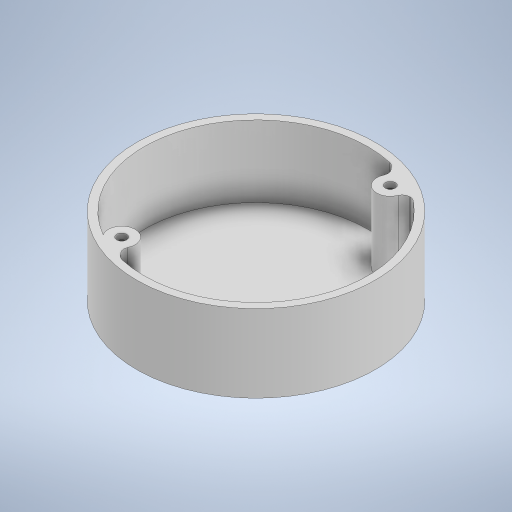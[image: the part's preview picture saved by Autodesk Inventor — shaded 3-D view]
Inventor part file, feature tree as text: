
AUTODESK INVENTOR PART (.ipt)
format: ipt  version: 2023 (Build 270158000, 158)  size: 305,152 bytes
history: native  units: in
note: dims shown in document units (in); Inventor stores cm internally (conversion verified against a paired STEP export)
features: sketch x7, extrude x5, fillet x3, hole x1
ambient origin geometry x8: Origin, YZ Plane, XZ Plane, XY Plane, X Axis, Y Axis, Z Axis, Center Point
bodies: Solid1 (feature_tree)
feature tree (16):
  extrude  "Extrusion1"  Depth=0.1in TaperAngle=0.0deg
  extrude  "Extrusion2"  Depth=4.0in
  extrude  "Extrusion3"  Depth=1.2in
  extrude  "Extrusion4"  Depth=0.45in
  fillet  "Fillet1"  Radius=0.45in
  hole  "Hole1"  [1 undecoded]
  sketch  "Sketch6"  dims[d17=0.125in]
  extrude  "Extrusion5"  Depth=0.125in
  fillet  "Fillet2"  Radius=1.2in
  fillet  "Fillet3"  Radius=0.125in
  sketch  "Sketch1"  dims[d0=4.0in d1=0.1in d2=0.0in]
  sketch  "Sketch2"  dims[d3=3.75in d4=4.0in]
  sketch  "Sketch3"  dims[d5=1.2in d6=0.0in d9=1.5in]
  sketch  "Sketch4"  dims[d10=0.75in d11=0.45in d12=0.45in]
  sketch  "Sketch5"  dims[d13=1.2in d14=0.0in d15=1.2in d16=0.0in]
  sketch  "Sketch7"  dims[d18=0.169in d19=0.75in d20=0.315in d21=0.157in d22=90.0deg d23=1.0in d24=0.8108in d25=0.3in d26=1.2in d27=0.0in d28=0.125in d29=0.125in]
note: 1 required parameter value undecoded (feature->parameter linkage not recoverable at this tier; creation-order binding heuristic only, values carry confidence <= 0.55)
